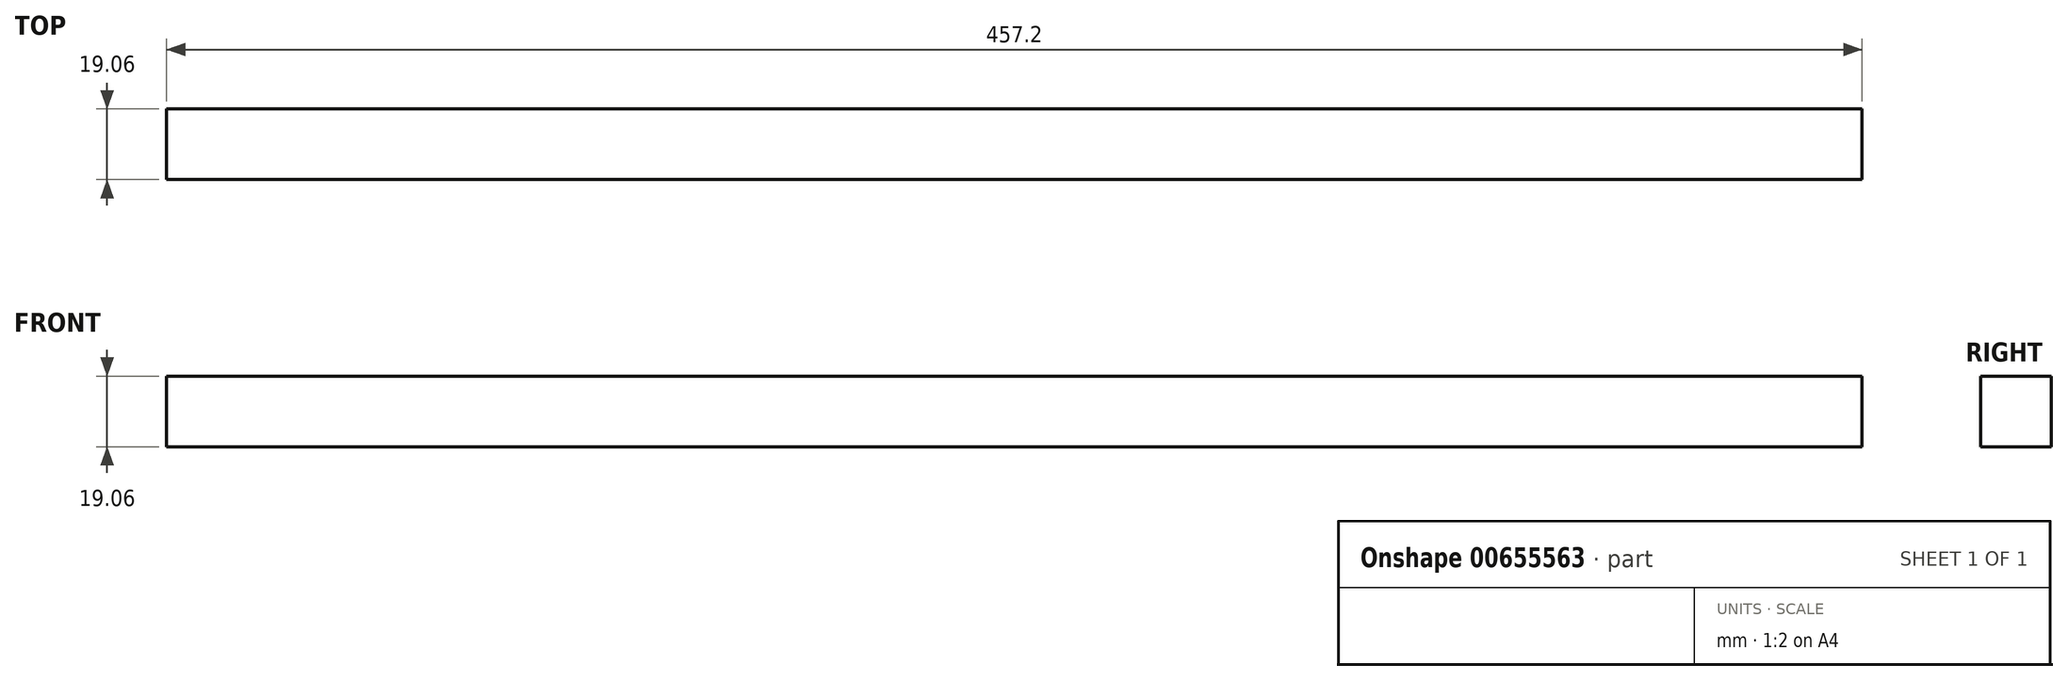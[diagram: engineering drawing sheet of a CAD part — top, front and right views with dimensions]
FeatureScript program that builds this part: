
annotation { "Feature Type Name" : "Feature", "Feature Type Description" : "" }
export const myFeature = defineFeature(function(context is Context, id is Id, definition is map)
    precondition{}
    {
        {
            var Q0;
            Q0=qCreatedBy(makeId("Front.planeOp"),FACE);
            var sketch = newSketch(context, id + "F0", { "sketchPlane" : qUnion([Q0])});
            skLineSegment(sketch, "E0.bottom", {"start": v(-228.6, 9.53) * mm, "end": v(228.6, 9.53) * mm});
            skLineSegment(sketch, "E0.top", {"start": v(-228.6, -9.52) * mm, "end": v(228.6, -9.52) * mm});
            skLineSegment(sketch, "E0.left", {"start": v(-228.6, 9.53) * mm, "end": v(-228.6, -9.52) * mm});
            skLineSegment(sketch, "E0.right", {"start": v(228.6, 9.53) * mm, "end": v(228.6, -9.52) * mm});
            skPoint(sketch, "E0.middle", {"position": v(0, 0) * mm});
            skSolve(sketch);
        }
        {
            var Q0;
            Q0=makeQuery(id+"F0.imprint","IMPRINT",FACE,{"disambiguationData":[TD([[makeQuery(id+"F0.imprint","IMPRINT",EDGE,{"derivedFrom":sQuery(id+"F0.wireOp",EDGE,"E0.bottom")}),-1.0]])]});
            extrude(context, id + "F1", {"entities" : qUnion([Q0]), "endBound" : BoundingType.SYMMETRIC, "depth" : 19.05 * mm, "offsetDistance" : 25.4 * mm});
        }
    });
